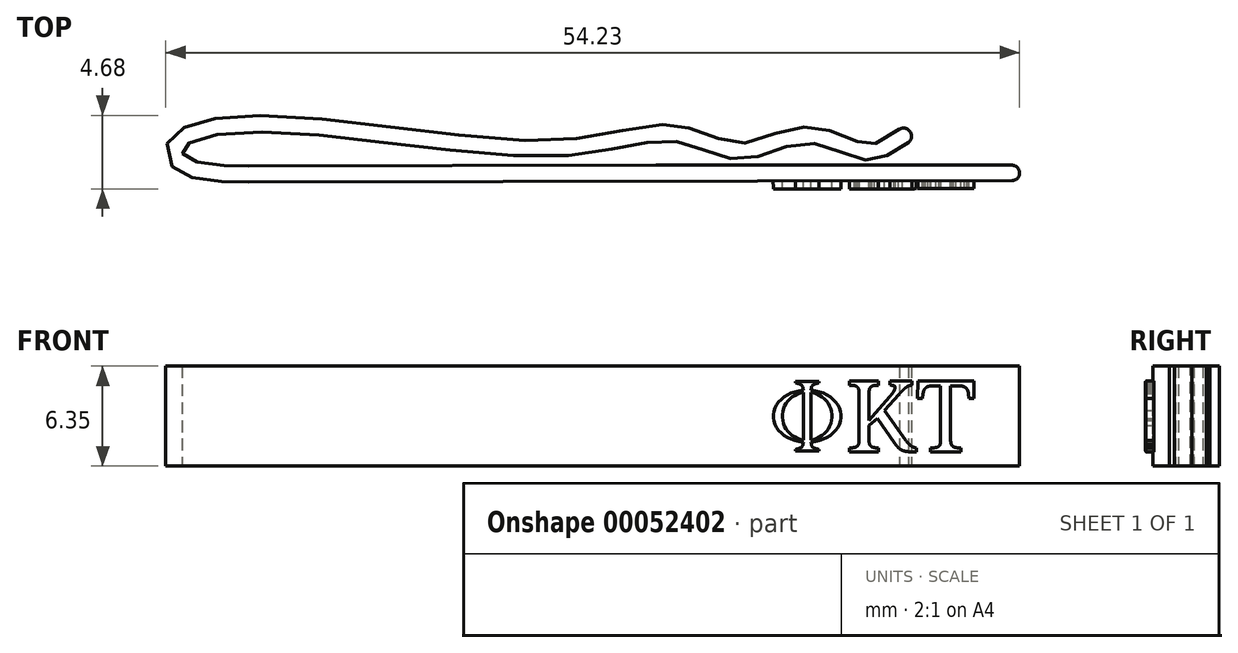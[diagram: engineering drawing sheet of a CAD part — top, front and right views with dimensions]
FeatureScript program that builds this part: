
annotation { "Feature Type Name" : "Feature", "Feature Type Description" : "" }
export const myFeature = defineFeature(function(context is Context, id is Id, definition is map)
    precondition{}
    {
        {
            var Q0;
            Q0=qCreatedBy(makeId("Top.planeOp"),FACE);
            var sketch = newSketch(context, id + "F0", { "sketchPlane" : qUnion([Q0])});
            skLineSegment(sketch, "E0.1", {"start": v(25.46, -0.76) * mm, "end": v(25.52, -0.75) * mm});
            skLineSegment(sketch, "E1", {"start": v(-76.32, -0.75) * mm, "end": v(-76.26, -0.76) * mm});
            skFitSpline(sketch, "E2.MirrorCS", {"points": [v(-57.5, -0.3) * mm, v(-60.97, 0) * mm, v(-61.73, 0.71) * mm, v(-57.55, 1.86) * mm, v(-37.6, 0.34) * mm, v(-30.36, 1.25) * mm, v(-26.28, 0.1) * mm, v(-21.95, 1.16) * mm, v(-18.26, 0.07) * mm, v(-15.61, 1.19) * mm], "startDerivative": vector(-28.24, 0) * mm, "endDerivative": vector(33.01, 22.26) * mm});
            skLineSegment(sketch, "E3.MirrorCS", {"start": v(-31.63, -0.25) * mm, "end": v(-9.03, -0.25) * mm});
            skLineSegment(sketch, "E4.MirrorCS", {"start": v(-31.63, -0.25) * mm, "end": v(-57.5, -0.3) * mm});
            skFitSpline(sketch, "E5.0", {"points": [v(-57.5, -1.31) * mm, v(-57.65, -1.31) * mm, v(-57.99, -1.31) * mm, v(-58.6, -1.3) * mm, v(-59.27, -1.28) * mm, v(-59.97, -1.23) * mm, v(-60.54, -1.15) * mm, v(-60.98, -1.05) * mm, v(-61.3, -0.96) * mm, v(-61.62, -0.84) * mm, v(-61.91, -0.68) * mm, v(-62.2, -0.49) * mm, v(-62.45, -0.23) * mm, v(-62.68, 0.14) * mm, v(-62.77, 0.57) * mm, v(-62.73, 0.93) * mm, v(-62.63, 1.26) * mm, v(-62.42, 1.56) * mm, v(-62.15, 1.82) * mm, v(-61.86, 2.01) * mm, v(-61.56, 2.17) * mm, v(-61.12, 2.35) * mm, v(-60.5, 2.53) * mm, v(-59.62, 2.7) * mm, v(-58.62, 2.83) * mm, v(-57.13, 2.9) * mm, v(-55.02, 2.85) * mm, v(-52.21, 2.6) * mm, v(-49.22, 2.26) * mm, v(-46.17, 1.89) * mm, v(-43.17, 1.56) * mm, v(-40.36, 1.34) * mm, v(-38.28, 1.31) * mm, v(-36.85, 1.41) * mm, v(-35.53, 1.58) * mm, v(-34.07, 1.86) * mm, v(-32.76, 2.15) * mm, v(-31.72, 2.29) * mm, v(-31.07, 2.32) * mm, v(-30.54, 2.3) * mm, v(-30.14, 2.25) * mm, v(-29.75, 2.17) * mm, v(-29.26, 2.03) * mm, v(-28.69, 1.83) * mm, v(-28.06, 1.58) * mm, v(-27.48, 1.36) * mm, v(-26.96, 1.2) * mm, v(-26.5, 1.12) * mm, v(-26.1, 1.12) * mm, v(-25.61, 1.22) * mm, v(-25.04, 1.4) * mm, v(-24.41, 1.63) * mm, v(-23.73, 1.88) * mm, v(-23.11, 2.05) * mm, v(-22.58, 2.15) * mm, v(-22.17, 2.18) * mm, v(-21.74, 2.18) * mm, v(-21.33, 2.13) * mm, v(-20.93, 2.04) * mm, v(-20.44, 1.9) * mm, v(-19.88, 1.7) * mm, v(-19.27, 1.43) * mm, v(-18.83, 1.26) * mm, v(-18.53, 1.16) * mm, v(-18.34, 1.1) * mm, v(-18.19, 1.08) * mm, v(-18.02, 1.08) * mm, v(-17.8, 1.1) * mm, v(-17.5, 1.21) * mm, v(-17, 1.47) * mm, v(-16.53, 1.8) * mm, v(-16.18, 2.03) * mm]});
            skLineSegment(sketch, "E6", {"start": v(-57.5, -1.31) * mm, "end": v(-9.03, -1.23) * mm});
            skArc(sketch, "E7", {"start": v(-9.03, -1.23) * mm, "mid": v(-8.54, -0.74) * mm, "end": v(-9.03, -0.25) * mm});
            skArc(sketch, "E8", {"start": v(-15.61, 1.19) * mm, "mid": v(-15.5, 1.88) * mm, "end": v(-16.18, 2.03) * mm});
            skSolve(sketch);
        }
        {
            var Q0;
            Q0 = qSketchRegion(id + "F0", true);
            extrude(context, id + "F1", {"entities" : qUnion([Q0]), "depth" : 6.35 * mm});
        }
        {
            var Q0;
            Q0=makeQuery(id+"F1.opExtrude","SWEPT_FACE",FACE,{"disambiguationData":[OSD([sQuery(id+"F0.wireOp",EDGE,"E6")])]});
            var sketch = newSketch(context, id + "F2", { "sketchPlane" : qUnion([Q0])});
            skPoint(sketch, "E9.rect.middle", {"position": v(-15.5, 3.18) * mm});
            skText(sketch, "E10", { "text": "KT", "fontName": "NotoSerif-Regular.ttf"});
            skLineSegment(sketch, "E11", {"start": v(-19.58, 0.9) * mm, "end": v(-23.32, 0.9) * mm});
            skLineSegment(sketch, "E12", {"start": v(-22.03, 5.4) * mm, "end": v(-21.28, 5.4) * mm});
            skLineSegment(sketch, "E13", {"start": v(-21.28, 5.4) * mm, "end": v(-21.28, 5.28) * mm});
            skPoint(sketch, "E14.endSnap0", {"position": v(-22.03, 3.18) * mm});
            skLineSegment(sketch, "E15.MirrorCS", {"start": v(-22.03, 0.96) * mm, "end": v(-21.28, 0.96) * mm});
            skLineSegment(sketch, "E16.MirrorCS", {"start": v(-21.28, 0.96) * mm, "end": v(-21.28, 1.07) * mm});
            skEllipse(sketch, "E17", {"center": v(-22.03, 3.18) * mm, "majorRadius": 2.16 * mm, "minorRadius": 1.67 * mm, "majorAxis": v(1, 0)});
            skLineSegment(sketch, "E18.MirrorCS", {"start": v(-22.03, 5.4) * mm, "end": v(-22.78, 5.4) * mm});
            skLineSegment(sketch, "E19.MirrorCS", {"start": v(-22.78, 5.4) * mm, "end": v(-22.78, 5.28) * mm});
            skLineSegment(sketch, "E20.MirrorCS", {"start": v(-22.03, 0.96) * mm, "end": v(-22.78, 0.96) * mm});
            skLineSegment(sketch, "E21.MirrorCS", {"start": v(-22.78, 0.96) * mm, "end": v(-22.78, 1.07) * mm});
            skFitSpline(sketch, "E22", {"points": [v(-22.78, 5.28) * mm, v(-22.4, 5.14) * mm, v(-22.3, 4.95) * mm, v(-22.28, 4.83) * mm], "startDerivative": vector(0.8, -0.08) * mm, "endDerivative": vector(0.03, -0.36) * mm});
            skLineSegment(sketch, "E23", {"start": v(-22.03, 5.4) * mm, "end": v(-22.03, 5.31) * mm});
            skFitSpline(sketch, "E24.MirrorCS", {"points": [v(-21.28, 5.28) * mm, v(-21.67, 5.14) * mm, v(-21.77, 4.95) * mm, v(-21.78, 4.83) * mm], "startDerivative": vector(-0.8, -0.08) * mm, "endDerivative": vector(-0.03, -0.36) * mm});
            skLineSegment(sketch, "E25", {"start": v(-21.78, 4.68) * mm, "end": v(-21.78, 1.67) * mm});
            skLineSegment(sketch, "E26", {"start": v(-22.28, 4.68) * mm, "end": v(-22.28, 1.67) * mm});
            skLineSegment(sketch, "E27", {"start": v(-21.78, 3.18) * mm, "end": v(-21.54, 3.18) * mm});
            skFitSpline(sketch, "E28.MirrorCS", {"points": [v(-21.28, 1.07) * mm, v(-21.67, 1.2) * mm, v(-21.77, 1.4) * mm, v(-21.78, 1.52) * mm], "startDerivative": vector(-0.8, 0.08) * mm, "endDerivative": vector(-0.03, 0.36) * mm});
            skFitSpline(sketch, "E29.MirrorCS", {"points": [v(-22.78, 1.07) * mm, v(-22.4, 1.2) * mm, v(-22.3, 1.4) * mm, v(-22.28, 1.52) * mm], "startDerivative": vector(0.8, 0.08) * mm, "endDerivative": vector(0.03, 0.36) * mm});
            skArc(sketch, "E30", {"start": v(-22.28, 4.68) * mm, "mid": v(-23.6, 3.18) * mm, "end": v(-22.28, 1.67) * mm});
            skArc(sketch, "E31.MirrorCS", {"start": v(-21.78, 4.68) * mm, "mid": v(-20.46, 3.18) * mm, "end": v(-21.78, 1.67) * mm});
            const initialGuessF2  = {"E10": [-0.01958, 0.0009, 1, 0, 0.00454]};
            skSetInitialGuess(sketch, initialGuessF2);
            skSolve(sketch);
        }
        {
            var Q0;
            Q0 = qSketchRegion(id + "F2", true);
            extrude(context, id + "F3", {"entities" : qUnion([Q0]), "operationType" : NewBodyOperationType.ADD, "depth" : 0.5 * mm});
        }
    });
